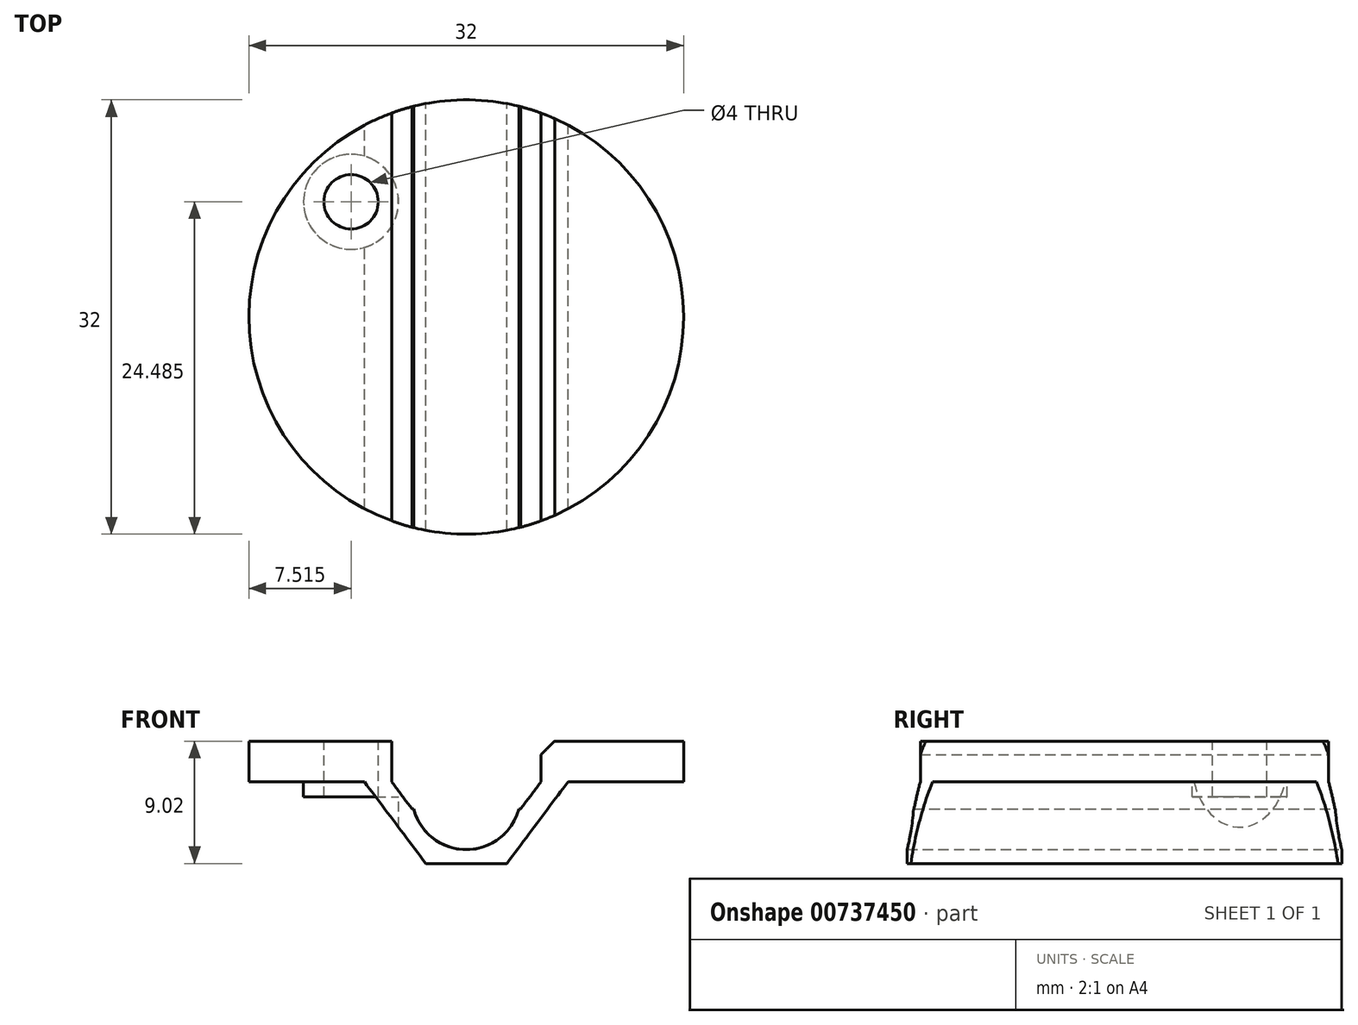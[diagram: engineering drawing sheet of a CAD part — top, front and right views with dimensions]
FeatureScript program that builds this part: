
annotation { "Feature Type Name" : "Feature", "Feature Type Description" : "" }
export const myFeature = defineFeature(function(context is Context, id is Id, definition is map)
    precondition{}
    {
        {
            var Q0;
            Q0=qCreatedBy(makeId("Front.planeOp"),FACE);
            var sketch = newSketch(context, id + "F0", { "sketchPlane" : qUnion([Q0])});
            skCircle(sketch, "E0", {"center": v(0, 0) * mm, "radius": 4 * mm});
            skLineSegment(sketch, "E1.bottom", {"start": v(-16, 4) * mm, "end": v(16, 4) * mm});
            skLineSegment(sketch, "E1.top", {"start": v(-16, 1) * mm, "end": v(16, 1) * mm});
            skLineSegment(sketch, "E1.left", {"start": v(-16, 4) * mm, "end": v(-16, 1) * mm});
            skLineSegment(sketch, "E1.right", {"start": v(16, 4) * mm, "end": v(16, 1) * mm});
            skLineSegment(sketch, "E2.top", {"start": v(-5.5, -5.02) * mm, "end": v(5.5, -5.02) * mm});
            skLineSegment(sketch, "E2.left", {"start": v(-5.5, -1) * mm, "end": v(-5.5, -5.02) * mm});
            skLineSegment(sketch, "E2.right", {"start": v(5.5, -1) * mm, "end": v(5.5, -5.02) * mm});
            skLineSegment(sketch, "E3", {"start": v(-5.5, 1) * mm, "end": v(-5.5, 4) * mm});
            skLineSegment(sketch, "E4", {"start": v(5.5, 4) * mm, "end": v(5.5, 1) * mm});
            skLineSegment(sketch, "E5", {"start": v(-5.5, -1) * mm, "end": v(5.5, -1) * mm});
            skLineSegment(sketch, "E6", {"start": v(-5.5, 1) * mm, "end": v(-5.5, 1) * mm});
            skLineSegment(sketch, "E7", {"start": v(-5.5, 1) * mm, "end": v(-4, -1) * mm});
            skLineSegment(sketch, "E8", {"start": v(-7.5, 1) * mm, "end": v(-2.98, -5.02) * mm});
            skLineSegment(sketch, "E9.MirrorCS", {"start": v(7.5, 1) * mm, "end": v(2.98, -5.02) * mm});
            skLineSegment(sketch, "E10.MirrorCS", {"start": v(5.5, 1) * mm, "end": v(4, -1) * mm});
            skLineSegment(sketch, "E11.MirrorCS", {"start": v(5.5, 1) * mm, "end": v(5.5, 1) * mm});
            skLineSegment(sketch, "E12", {"start": v(0, 0) * mm, "end": v(0, 8.7) * mm, "construction": true});
            skPoint(sketch, "E12.endSnap0", {"position": v(0, 1) * mm});
            skSolve(sketch);
        }
        {
            var Q0;
            {var subQ0=sQuery(id+"F0.wireOp",EDGE,"E1.left");Q0=makeQuery(id+"F0.imprint","IMPRINT",FACE,{"disambiguationData":[TD([[makeQuery(id+"F0.imprint","IMPRINT",EDGE,{"derivedFrom":subQ0}),1.0]])]});}
            var Q1;
            Q1=sQuery(id+"F0.wireOp",EDGE,"E12");
            revolve(context, id + "F1", {"surfaceOperationType" : NewSurfaceOperationType.NEW, "entities" : qUnion([Q0]), "axis" : qUnion([Q1]), "revolveType" : RevolveType.FULL});
        }
        {
            var Q0;
            {var subQ0=sQuery(id+"F0.wireOp",EDGE,"E6");Q0=makeQuery(id+"F0.imprint","IMPRINT",FACE,{"disambiguationData":[TD([[makeQuery(id+"F0.imprint","IMPRINT",EDGE,{"derivedFrom":subQ0}),-1.0]])]});}
            var Q1;
            {var subQ0=sQuery(id+"F0.wireOp",EDGE,"E5");var subQ10=sQuery(id+"F0.wireOp",EDGE,"E0");var subQ15=makeQuery(id+"F0.imprint","INTERSECT",VERTEX,{"disambiguationData":[OD(0.0)],"derivedFrom":[subQ10,subQ0]});Q1=makeQuery(id+"F0.imprint","IMPRINT",FACE,{"disambiguationData":[TD([[makeQuery(id+"F0.imprint","IMPRINT",EDGE,{"disambiguationData":[TD([[subQ15,-1.0]])],"derivedFrom":subQ10}),-1.0]])]});}
            var Q2;
            {var subQ8=sQuery(id+"F0.wireOp",EDGE,"E10.MirrorCS");Q2=makeQuery(id+"F0.imprint","IMPRINT",FACE,{"disambiguationData":[TD([[makeQuery(id+"F0.imprint","IMPRINT",EDGE,{"derivedFrom":subQ8}),1.0]])]});}
            var Q3;
            Q3=makeQuery(id+"F1.opRevolve","SWEPT_FACE",FACE,{"disambiguationData":[OSD([sQuery(id+"F0.wireOp",EDGE,"E1.left")])]});
            var Q4;
            Q4=makeQuery(id+"F1.opRevolve","SWEPT_FACE",FACE,{"disambiguationData":[OSD([sQuery(id+"F0.wireOp",EDGE,"E1.left")])]});
            extrude(context, id + "F2", {"entities" : qUnion([Q0, Q1, Q2]), "operationType" : NewBodyOperationType.ADD, "endBound" : BoundingType.UP_TO_SURFACE, "depth" : 25 * mm, "endBoundEntityFace" : qUnion([Q3]), "offsetDistance" : 25 * mm, "hasSecondDirection" : true, "secondDirectionBound" : SecondDirectionBoundingType.UP_TO_SURFACE, "secondDirectionOppositeDirection" : true, "secondDirectionDepth" : 25 * mm, "secondDirectionBoundEntityFace" : qUnion([Q4])});
        }
        {
            var Q0;
            {var subQ5=sQuery(id+"F0.wireOp",EDGE,"E4");Q0=makeQuery(id+"F0.imprint","IMPRINT",FACE,{"disambiguationData":[TD([[makeQuery(id+"F0.imprint","IMPRINT",EDGE,{"derivedFrom":subQ5}),-1.0]])]});}
            var Q1;
            {var subQ5=sQuery(id+"F0.wireOp",EDGE,"E3");Q1=makeQuery(id+"F0.imprint","IMPRINT",FACE,{"disambiguationData":[TD([[makeQuery(id+"F0.imprint","IMPRINT",EDGE,{"derivedFrom":subQ5}),-1.0]])]});}
            var Q2;
            {var subQ0=sQuery(id+"F0.wireOp",EDGE,"E0");var subQ1=makeQuery(id+"F0.imprint","INTERSECT",VERTEX,{"derivedFrom":[subQ0,sQuery(id+"F0.wireOp",EDGE,"E1.bottom")]});Q2=makeQuery(id+"F0.imprint","IMPRINT",FACE,{"disambiguationData":[TD([[makeQuery(id+"F0.imprint","IMPRINT",EDGE,{"disambiguationData":[TD([[subQ1,1.0]])],"derivedFrom":subQ0}),1.0]])]});}
            extrude(context, id + "F3", {"entities" : qUnion([Q0, Q1, Q2]), "operationType" : NewBodyOperationType.REMOVE, "endBound" : BoundingType.THROUGH_ALL, "oppositeDirection" : true, "depth" : 25 * mm, "offsetDistance" : 25 * mm, "hasSecondDirection" : true, "secondDirectionBound" : SecondDirectionBoundingType.THROUGH_ALL, "secondDirectionOppositeDirection" : false, "secondDirectionDepth" : 25 * mm});
        }
        {
            var Q0;
            Q0=makeQuery(id+"F3.boolean.opBoolean","COPY",EDGE,{"derivedFrom":makeQuery(id+"F3.opExtrude","SWEPT_EDGE",EDGE,{"disambiguationData":[OSD([sQuery(id+"F0.wireOp",EDGE,"E1.bottom"),sQuery(id+"F0.wireOp",EDGE,"E4")])]})});
            var Q1;
            Q1=makeQuery(id+"F3.boolean.opBoolean","COPY",EDGE,{"derivedFrom":makeQuery(id+"F3.opExtrude","SWEPT_EDGE",EDGE,{"disambiguationData":[OSD([sQuery(id+"F0.wireOp",EDGE,"E1.bottom"),sQuery(id+"F0.wireOp",EDGE,"E3")])]})});
            chamfer(context, id + "F4", {"entities" : qUnion([Q0, Q1]), "width" : 1 * mm, "tangentPropagation" : true});
        }
        {
            var Q0;
            Q0=makeQuery(id+"F3.boolean.opBoolean","SPLIT",FACE,{"disambiguationData":[TD([makeQuery(id+"F2.opExtrude","SWEPT_FACE",FACE,{"disambiguationData":[OSD([sQuery(id+"F0.wireOp",EDGE,"E6")])]})])],"derivedFrom":makeQuery(id+"F1.opRevolve","SWEPT_FACE",FACE,{"disambiguationData":[OSD([sQuery(id+"F0.wireOp",EDGE,"E1.bottom")])]})});
            var sketch = newSketch(context, id + "F5", { "sketchPlane" : qUnion([Q0])});
            skPoint(sketch, "E13", {"position": v(-8.49, 8.49) * mm});
            skLineSegment(sketch, "E14", {"start": v(0, 0) * mm, "end": v(-8.49, 8.49) * mm, "construction": true});
            skSolve(sketch);
        }
        {
            var Q0;
            {var subQ0=sQuery(id+"F0.wireOp",EDGE,"E1.left");Q0=makeQuery(id+"F2.boolean.opBoolean","SPLIT",FACE,{"disambiguationData":[TD([makeQuery(id+"F1.opRevolve","SWEPT_FACE",FACE,{"disambiguationData":[OSD([subQ0])]}),makeQuery(id+"F2.opExtrude","SWEPT_FACE",FACE,{"disambiguationData":[OSD([sQuery(id+"F0.wireOp",EDGE,"E8")])]}),makeQuery(id+"F2.opExtrude","CAP_FACE",FACE,{"disambiguationData":[OSD([subQ0]),OD(0.0)],"isStart":false}),makeQuery(id+"F2.opExtrude","CAP_FACE",FACE,{"disambiguationData":[OSD([subQ0]),OD(1.0)],"isStart":false})])],"derivedFrom":makeQuery(id+"F1.opRevolve","SWEPT_FACE",FACE,{"disambiguationData":[OSD([sQuery(id+"F0.wireOp",EDGE,"E1.top")])]})});}
            var sketch = newSketch(context, id + "F6", { "sketchPlane" : qUnion([Q0])});
            skArc(sketch, "E15", {"start": v(-5.99, -6.04) * mm, "mid": v(-11.99, -8.49) * mm, "end": v(-5.99, -10.93) * mm});
            skLineSegment(sketch, "E16", {"start": v(-5.99, -6.04) * mm, "end": v(-5.99, -10.93) * mm});
            skSolve(sketch);
        }
        {
            var Q0;
            Q0 = qSketchRegion(id + "F6", true);
            extrude(context, id + "F7", {"entities" : qUnion([Q0]), "operationType" : NewBodyOperationType.ADD, "depth" : 1.1 * mm, "offsetDistance" : 25 * mm});
        }
        {
            var Q0;
            Q0=makeQuery(id+"F7.opExtrude","CAP_FACE",FACE,{"disambiguationData":[OSD([sQuery(id+"F6.wireOp",EDGE,"E15"),sQuery(id+"F6.wireOp",EDGE,"E16")])],"isStart":false});
            var sketch = newSketch(context, id + "F8", { "sketchPlane" : qUnion([Q0])});
            skCircle(sketch, "E17.0", {"center": v(-8.49, -8.49) * mm, "radius": 3.5 * mm});
            skSolve(sketch);
        }
        {
            var Q0;
            Q0 = qSketchRegion(id + "F8", true);
            extrude(context, id + "F9", {"entities" : qUnion([Q0]), "operationType" : NewBodyOperationType.REMOVE, "endBound" : BoundingType.THROUGH_ALL, "depth" : 25 * mm, "offsetDistance" : 25 * mm});
        }
        {
            var Q0;
            Q0=sQuery(id+"F5.wireOp",VERTEX,"E13");
            var Q1;
            Q1=makeQuery(id+"F1.opRevolve","SWEPT_BODY",BODY,{"disambiguationData":[OSD([sQuery(id+"F0.wireOp",EDGE,"E1.bottom"),sQuery(id+"F0.wireOp",EDGE,"E1.top"),sQuery(id+"F0.wireOp",EDGE,"E1.left"),sQuery(id+"F0.wireOp",EDGE,"E3")])]});
            hole(context, id + "F10", {"style" : HoleStyle.SIMPLE, "endStyle" : HoleEndStyle.THROUGH, "holeDiameter" : 4 * mm, "majorDiameter" : 5 * mm, "isTappedThrough" : true, "tappedDepth" : 12 * mm, "tapClearance" : 3, "locations" : qUnion([Q0]), "scope" : qUnion([Q1])});
        }
    });
